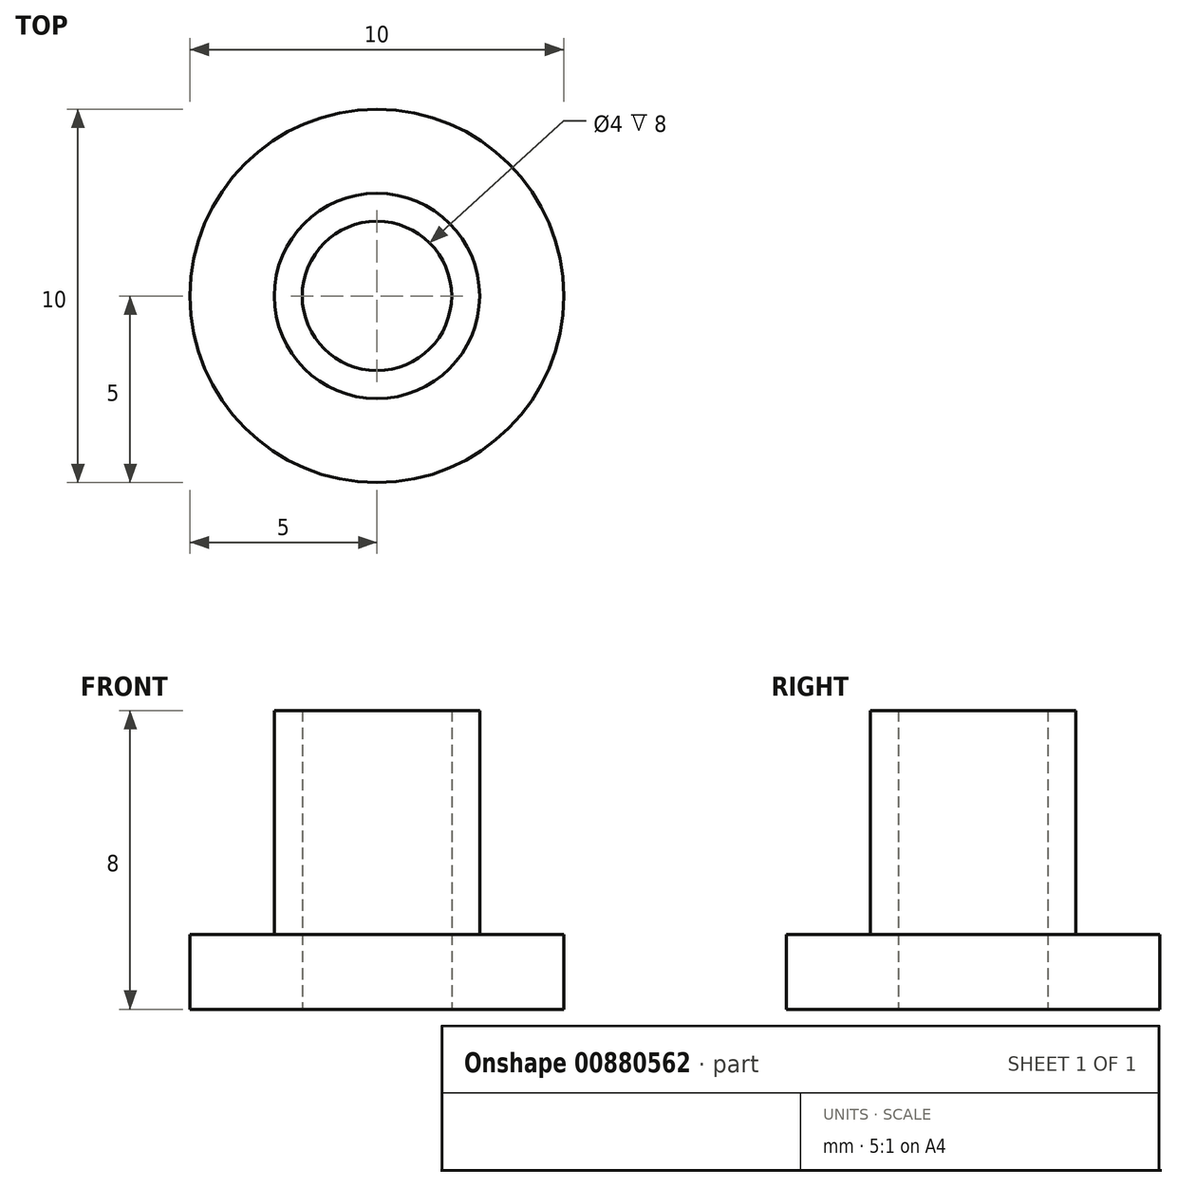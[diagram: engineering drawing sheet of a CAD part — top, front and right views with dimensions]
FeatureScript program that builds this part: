
annotation { "Feature Type Name" : "Feature", "Feature Type Description" : "" }
export const myFeature = defineFeature(function(context is Context, id is Id, definition is map)
    precondition{}
    {
        {
            var Q0;
            Q0=qCreatedBy(makeId("Right.planeOp"),FACE);
            var sketch = newSketch(context, id + "F0", { "sketchPlane" : qUnion([Q0])});
            skLineSegment(sketch, "E0", {"start": v(0, 0) * mm, "end": v(0, 13.77) * mm, "construction": true});
            skLineSegment(sketch, "E1", {"start": v(2, 0) * mm, "end": v(2, 8) * mm});
            skLineSegment(sketch, "E2", {"start": v(2, 8) * mm, "end": v(2.75, 8) * mm});
            skLineSegment(sketch, "E3", {"start": v(2.75, 8) * mm, "end": v(2.75, 2) * mm});
            skLineSegment(sketch, "E4", {"start": v(2.75, 2) * mm, "end": v(5, 2) * mm});
            skLineSegment(sketch, "E5", {"start": v(5, 2) * mm, "end": v(5, 0) * mm});
            skLineSegment(sketch, "E6", {"start": v(5, 0) * mm, "end": v(2, 0) * mm});
            skSolve(sketch);
        }
        {
            var Q0;
            Q0 = qSketchRegion(id + "F0", true);
            var Q1;
            Q1=sQuery(id+"F0.wireOp",EDGE,"E0");
            revolve(context, id + "F1", {"surfaceOperationType" : NewSurfaceOperationType.NEW, "entities" : qUnion([Q0]), "axis" : qUnion([Q1]), "revolveType" : RevolveType.FULL});
        }
    });
